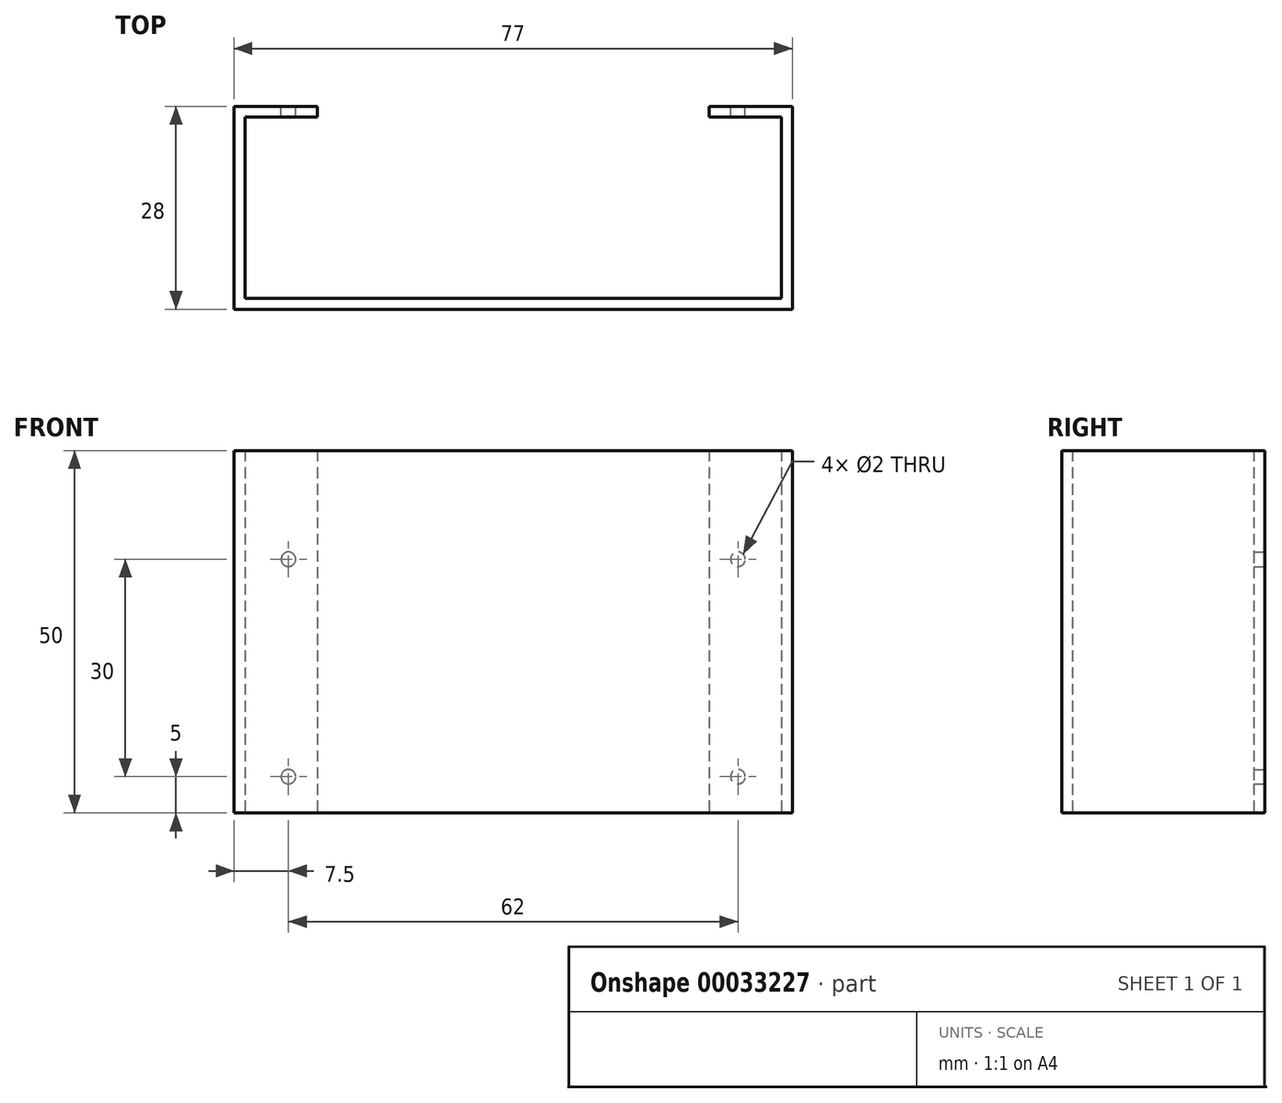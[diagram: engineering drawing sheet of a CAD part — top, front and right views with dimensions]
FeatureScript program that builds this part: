
annotation { "Feature Type Name" : "Feature", "Feature Type Description" : "" }
export const myFeature = defineFeature(function(context is Context, id is Id, definition is map)
    precondition{}
    {
        {
            var Q0;
            Q0=qCreatedBy(makeId("Top.planeOp"),FACE);
            var sketch = newSketch(context, id + "F0", { "sketchPlane" : qUnion([Q0])});
            skLineSegment(sketch, "E0.bottom", {"start": v(-38.5, 14) * mm, "end": v(-27, 14) * mm});
            skLineSegment(sketch, "E0.top", {"start": v(-38.5, -14) * mm, "end": v(38.5, -14) * mm});
            skLineSegment(sketch, "E0.left", {"start": v(-38.5, 14) * mm, "end": v(-38.5, -14) * mm});
            skLineSegment(sketch, "E0.right", {"start": v(38.5, 14) * mm, "end": v(38.5, -14) * mm});
            skPoint(sketch, "E0.middle", {"position": v(0, 0) * mm});
            skLineSegment(sketch, "E1", {"start": v(-27, 14) * mm, "end": v(-27, 12.5) * mm});
            skLineSegment(sketch, "E2", {"start": v(-27, 12.5) * mm, "end": v(-37, 12.5) * mm});
            skLineSegment(sketch, "E3", {"start": v(-37, 12.5) * mm, "end": v(-37, -12.5) * mm});
            skLineSegment(sketch, "E4", {"start": v(-37, -12.5) * mm, "end": v(0, -12.5) * mm});
            skLineSegment(sketch, "E5", {"start": v(-31, 14) * mm, "end": v(-31, 12.5) * mm, "construction": true});
            skLineSegment(sketch, "E6.MirrorCS", {"start": v(38.5, 14) * mm, "end": v(27, 14) * mm});
            skLineSegment(sketch, "E7.MirrorCS", {"start": v(27, 12.5) * mm, "end": v(37, 12.5) * mm});
            skLineSegment(sketch, "E8.MirrorCS", {"start": v(37, 12.5) * mm, "end": v(37, -12.5) * mm});
            skLineSegment(sketch, "E9.MirrorCS", {"start": v(37, -12.5) * mm, "end": v(0, -12.5) * mm});
            skLineSegment(sketch, "E10.MirrorCS", {"start": v(27, 14) * mm, "end": v(27, 12.5) * mm});
            skSolve(sketch);
        }
        {
            var Q0;
            Q0 = qSketchRegion(id + "F0", true);
            extrude(context, id + "F1", {"entities" : qUnion([Q0]), "depth" : 50 * mm});
        }
        {
            var Q0;
            Q0=makeQuery(id+"F1.opExtrude","SWEPT_FACE",FACE,{"disambiguationData":[OSD([sQuery(id+"F0.wireOp",EDGE,"E6.MirrorCS")])]});
            var sketch = newSketch(context, id + "F2", { "sketchPlane" : qUnion([Q0])});
            skCircle(sketch, "E11", {"center": v(-31, 5) * mm, "radius": 1 * mm});
            skCircle(sketch, "E12", {"center": v(-31, 35) * mm, "radius": 1 * mm});
            skCircle(sketch, "E13.MirrorC", {"center": v(31, 35) * mm, "radius": 1 * mm});
            skCircle(sketch, "E14.MirrorC", {"center": v(31, 5) * mm, "radius": 1 * mm});
            skSolve(sketch);
        }
        {
            var Q0;
            Q0 = qSketchRegion(id + "F2", true);
            extrude(context, id + "F3", {"entities" : qUnion([Q0]), "operationType" : NewBodyOperationType.REMOVE, "endBound" : BoundingType.UP_TO_NEXT, "oppositeDirection" : true, "depth" : 25 * mm});
        }
    });
